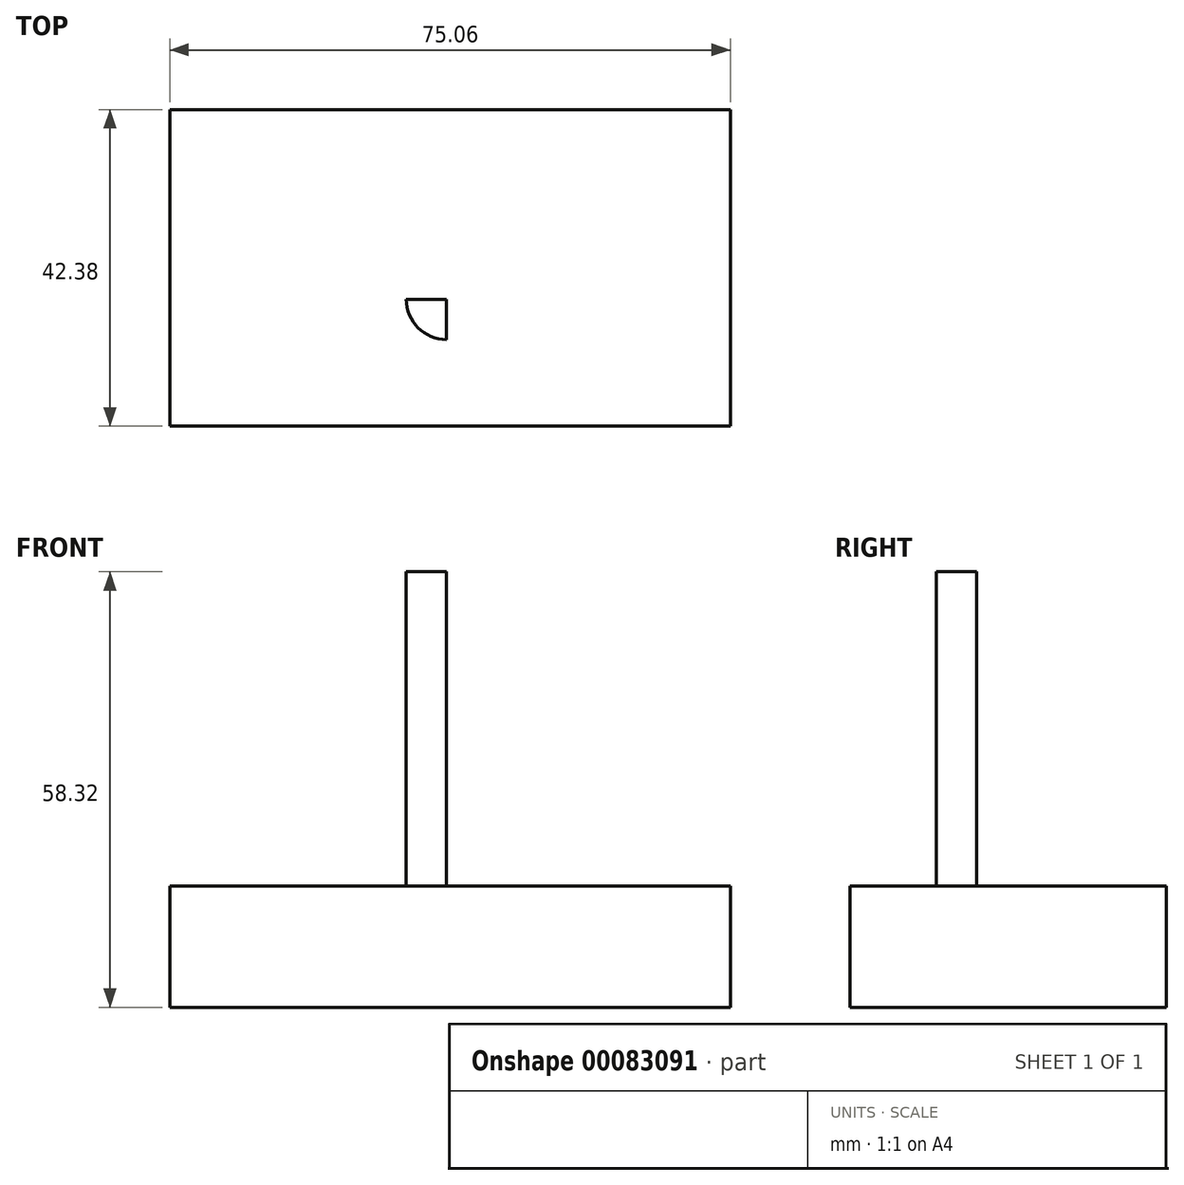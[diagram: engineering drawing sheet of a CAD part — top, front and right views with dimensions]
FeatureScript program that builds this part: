
annotation { "Feature Type Name" : "Feature", "Feature Type Description" : "" }
export const myFeature = defineFeature(function(context is Context, id is Id, definition is map)
    precondition{}
    {
        {
            var Q0;
            Q0=qCreatedBy(makeId("Front.planeOp"),FACE);
            var sketch = newSketch(context, id + "F0", { "sketchPlane" : qUnion([Q0])});
            skLineSegment(sketch, "E0.bottom", {"start": v(37.98, -8.2) * mm, "end": v(-37.08, -8.2) * mm});
            skLineSegment(sketch, "E0.top", {"start": v(37.98, 8) * mm, "end": v(-37.08, 8) * mm});
            skLineSegment(sketch, "E0.left", {"start": v(37.98, -8.2) * mm, "end": v(37.98, 8) * mm});
            skLineSegment(sketch, "E0.right", {"start": v(-37.08, -8.2) * mm, "end": v(-37.08, 8) * mm});
            skLineSegment(sketch, "E1", {"start": v(0, 8) * mm, "end": v(0, 49.59) * mm});
            skSolve(sketch);
        }
        {
            var Q0;
            Q0=makeQuery(id+"F0.imprint","IMPRINT",FACE,{"disambiguationData":[TD([[makeQuery(id+"F0.imprint","IMPRINT",EDGE,{"derivedFrom":sQuery(id+"F0.wireOp",EDGE,"E0.bottom")}),-1.0]])]});
            extrude(context, id + "F1", {"entities" : qUnion([Q0]), "depth" : 16.98 * mm, "hasSecondDirection" : true, "secondDirectionOppositeDirection" : true, "secondDirectionDepth" : 25.4 * mm});
        }
        {
            var Q0;
            Q0=qCreatedBy(makeId("Front.planeOp"),FACE);
            var sketch = newSketch(context, id + "F2", { "sketchPlane" : qUnion([Q0])});
            skLineSegment(sketch, "E2.bottom", {"start": v(-5.4, 0) * mm, "end": v(4.86, 0) * mm});
            skLineSegment(sketch, "E2.top", {"start": v(-5.4, 50.13) * mm, "end": v(4.86, 50.13) * mm});
            skLineSegment(sketch, "E2.left", {"start": v(-5.4, 0) * mm, "end": v(-5.4, 50.13) * mm});
            skLineSegment(sketch, "E2.right", {"start": v(4.86, 0) * mm, "end": v(4.86, 50.13) * mm});
            skLineSegment(sketch, "E3", {"start": v(0, 0) * mm, "end": v(0, 50.13) * mm});
            skSolve(sketch);
        }
        {
            var Q0;
            {var subQ0=sQuery(id+"F2.wireOp",EDGE,"E2.left");Q0=makeQuery(id+"F2.imprint","IMPRINT",FACE,{"disambiguationData":[TD([[makeQuery(id+"F2.imprint","IMPRINT",EDGE,{"derivedFrom":subQ0}),-1.0]])]});}
            var Q1;
            Q1=sQuery(id+"F2.wireOp",EDGE,"E3");
            revolve(context, id + "F3", {"operationType" : NewBodyOperationType.ADD, "entities" : qUnion([Q0]), "axis" : qUnion([Q1]), "revolveType" : RevolveType.ONE_DIRECTION, "angle" : 90 * degree});
        }
    });
